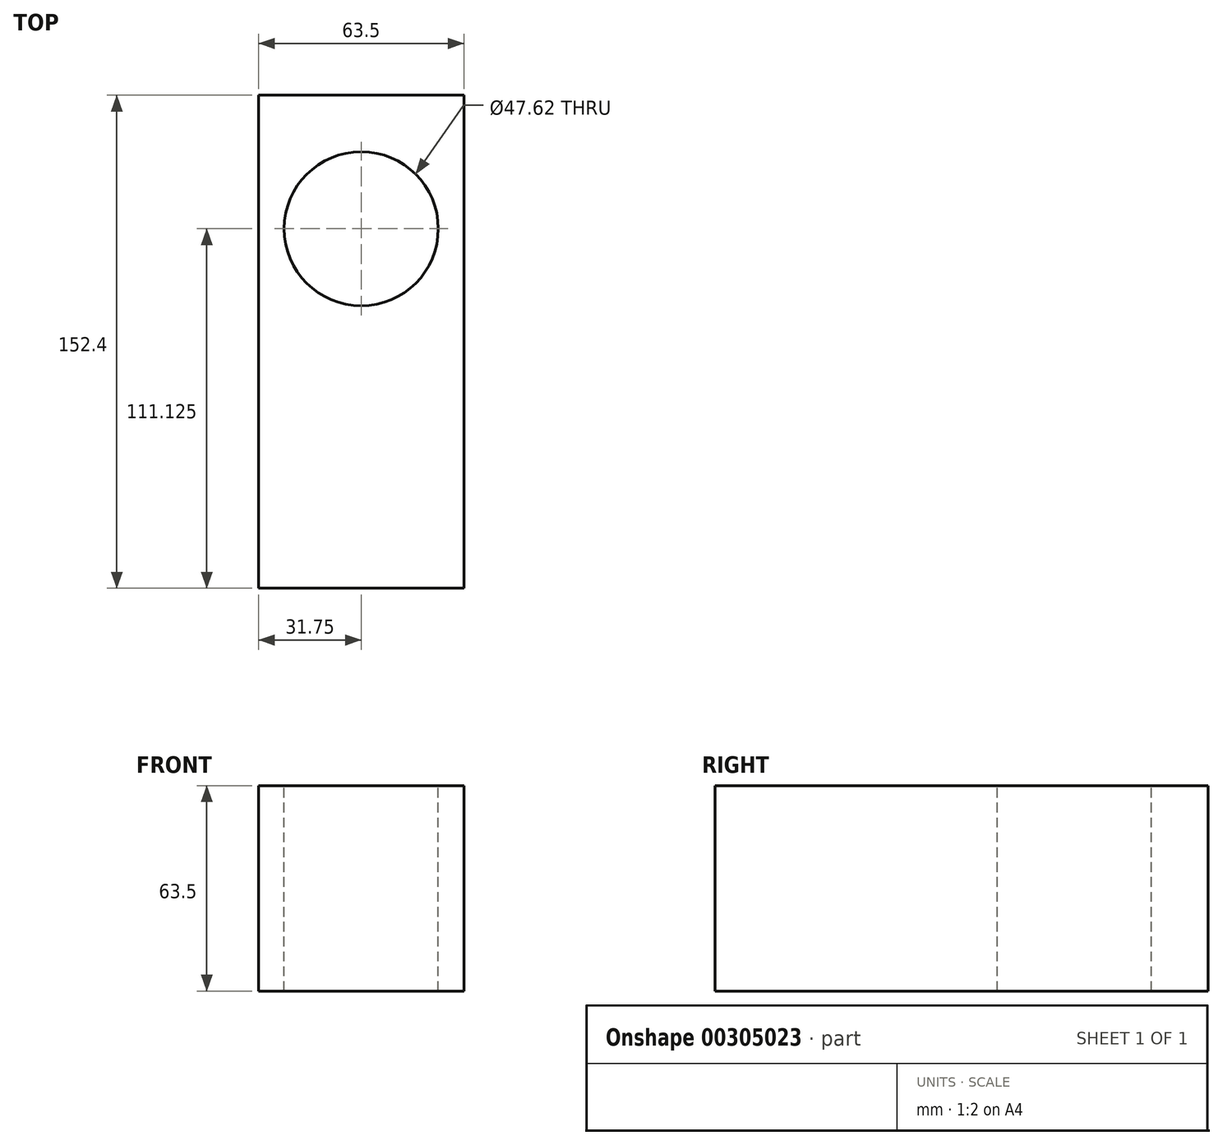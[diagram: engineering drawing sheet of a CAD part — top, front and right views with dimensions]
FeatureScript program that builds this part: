
annotation { "Feature Type Name" : "Feature", "Feature Type Description" : "" }
export const myFeature = defineFeature(function(context is Context, id is Id, definition is map)
    precondition{}
    {
        {
            var Q0;
            Q0=qCreatedBy(makeId("Right.planeOp"),FACE);
            var sketch = newSketch(context, id + "F0", { "sketchPlane" : qUnion([Q0])});
            skLineSegment(sketch, "E0", {"start": v(-76.2, 31.75) * mm, "end": v(76.2, 31.75) * mm});
            skLineSegment(sketch, "E1.MirrorCS", {"start": v(-76.2, -31.75) * mm, "end": v(76.2, -31.75) * mm});
            skLineSegment(sketch, "E2", {"start": v(76.2, 31.75) * mm, "end": v(76.2, -31.75) * mm});
            skLineSegment(sketch, "E3.MirrorCS", {"start": v(-76.2, 31.75) * mm, "end": v(-76.2, -31.75) * mm});
            skSolve(sketch);
        }
        {
            var Q0;
            Q0=makeQuery(id+"F0.imprint","IMPRINT",FACE,{"disambiguationData":[TD([[makeQuery(id+"F0.imprint","IMPRINT",EDGE,{"derivedFrom":sQuery(id+"F0.wireOp",EDGE,"E0")}),-1.0]])]});
            extrude(context, id + "F1", {"entities" : qUnion([Q0]), "endBound" : BoundingType.SYMMETRIC, "depth" : 63.5 * mm});
        }
        {
            var Q0;
            Q0=makeQuery(id+"F1.opExtrude","SWEPT_FACE",FACE,{"disambiguationData":[OSD([sQuery(id+"F0.wireOp",EDGE,"E0")])]});
            var sketch = newSketch(context, id + "F2", { "sketchPlane" : qUnion([Q0])});
            skPoint(sketch, "E4", {"position": v(0, 34.93) * mm});
            skSolve(sketch);
        }
        {
            var Q0;
            Q0=sQuery(id+"F2.wireOp",VERTEX,"E4");
            var Q1;
            Q1=makeQuery(id+"F1.opExtrude","SWEPT_BODY",BODY,{"disambiguationData":[OSD([sQuery(id+"F0.wireOp",EDGE,"E0"),sQuery(id+"F0.wireOp",EDGE,"E1.MirrorCS"),sQuery(id+"F0.wireOp",EDGE,"E2"),sQuery(id+"F0.wireOp",EDGE,"E3.MirrorCS")])]});
            hole(context, id + "F3", {"style" : HoleStyle.SIMPLE, "endStyle" : HoleEndStyle.THROUGH, "holeDiameter" : 47.62 * mm, "tappedDepth" : 12.7 * mm, "tapClearance" : 3, "locations" : qUnion([Q0]), "scope" : qUnion([Q1])});
        }
    });
